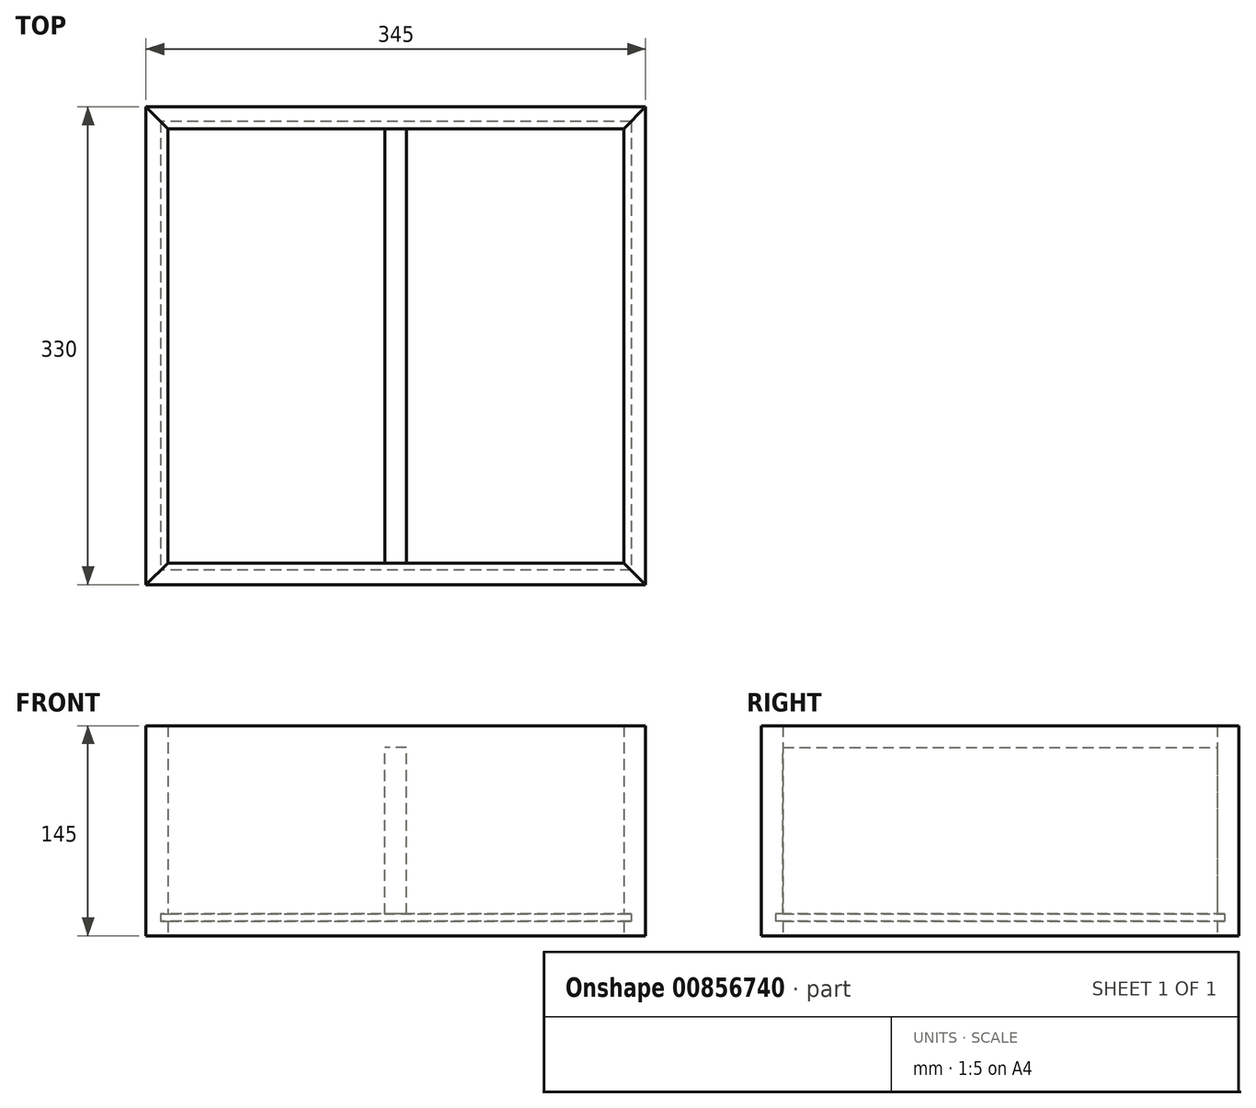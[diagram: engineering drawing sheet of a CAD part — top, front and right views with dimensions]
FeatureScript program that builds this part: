
annotation { "Feature Type Name" : "Feature", "Feature Type Description" : "" }
export const myFeature = defineFeature(function(context is Context, id is Id, definition is map)
    precondition{}
    {
        {
            var Q0;
            Q0=qCreatedBy(makeId("Front.planeOp"),FACE);
            var sketch = newSketch(context, id + "F0", { "sketchPlane" : qUnion([Q0])});
            skLineSegment(sketch, "E0", {"start": v(-172.5, 0) * mm, "end": v(172.5, 0) * mm, "construction": true});
            skLineSegment(sketch, "E1", {"start": v(172.5, 0) * mm, "end": v(172.5, 145) * mm, "construction": true});
            skLineSegment(sketch, "E2", {"start": v(172.5, 145) * mm, "end": v(-172.5, 145) * mm, "construction": true});
            skLineSegment(sketch, "E3", {"start": v(-172.5, 145) * mm, "end": v(-172.5, 0) * mm, "construction": true});
            skLineSegment(sketch, "E4", {"start": v(0, 145) * mm, "end": v(0, -38.8) * mm, "construction": true});
            skLineSegment(sketch, "E5", {"start": v(-172.5, 15) * mm, "end": v(172.5, 15) * mm, "construction": true});
            skLineSegment(sketch, "E6", {"start": v(-7.5, 130) * mm, "end": v(-7.5, 15) * mm, "construction": true});
            skLineSegment(sketch, "E7.MirrorCS", {"start": v(7.5, 130) * mm, "end": v(7.5, 15) * mm, "construction": true});
            skLineSegment(sketch, "E8", {"start": v(-157.5, 145) * mm, "end": v(-157.5, 0) * mm, "construction": true});
            skLineSegment(sketch, "E9", {"start": v(-7.5, 130) * mm, "end": v(7.5, 130) * mm, "construction": true});
            skLineSegment(sketch, "E10", {"start": v(-172.5, 130) * mm, "end": v(-157.5, 130) * mm, "construction": true});
            skLineSegment(sketch, "E11.MirrorCS", {"start": v(172.5, 130) * mm, "end": v(157.5, 130) * mm, "construction": true});
            skLineSegment(sketch, "E12.MirrorCS", {"start": v(157.5, 145) * mm, "end": v(157.5, 0) * mm, "construction": true});
            skLineSegment(sketch, "E13", {"start": v(-172.5, 10) * mm, "end": v(172.5, 10) * mm, "construction": true});
            skLineSegment(sketch, "E14", {"start": v(162.5, 15) * mm, "end": v(162.5, 10) * mm, "construction": true});
            skLineSegment(sketch, "E15.MirrorCS", {"start": v(-162.5, 15) * mm, "end": v(-162.5, 10) * mm, "construction": true});
            skSolve(sketch);
        }
        {
            var Q0;
            Q0=qCreatedBy(makeId("Right.planeOp"),FACE);
            var sketch = newSketch(context, id + "F1", { "sketchPlane" : qUnion([Q0])});
            skLineSegment(sketch, "E16", {"start": v(0, 0) * mm, "end": v(330, 0) * mm, "construction": true});
            skLineSegment(sketch, "E17", {"start": v(330, 0) * mm, "end": v(330, 145) * mm, "construction": true});
            skLineSegment(sketch, "E18", {"start": v(330, 145) * mm, "end": v(0, 145) * mm, "construction": true});
            skLineSegment(sketch, "E19", {"start": v(0, 130) * mm, "end": v(330, 130) * mm, "construction": true});
            skLineSegment(sketch, "E20", {"start": v(165, 145) * mm, "end": v(165, 0) * mm, "construction": true});
            skLineSegment(sketch, "E21", {"start": v(315, 145) * mm, "end": v(315, 0) * mm, "construction": true});
            skLineSegment(sketch, "E22.MirrorCS", {"start": v(15, 145) * mm, "end": v(15, 0) * mm, "construction": true});
            skLineSegment(sketch, "E23", {"start": v(330, 15) * mm, "end": v(0, 15) * mm, "construction": true});
            skLineSegment(sketch, "E24", {"start": v(330, 10) * mm, "end": v(0, 10) * mm, "construction": true});
            skLineSegment(sketch, "E25", {"start": v(320, 15) * mm, "end": v(320, 10) * mm, "construction": true});
            skLineSegment(sketch, "E26.MirrorCS", {"start": v(10, 15) * mm, "end": v(10, 10) * mm, "construction": true});
            skSolve(sketch);
        }
        {
            var Q0;
            Q0=qCreatedBy(makeId("Top.planeOp"),FACE);
            var Q1;
            Q1=sQuery(id+"F1.wireOp",VERTEX,"E25.end");
            cPlane(context, id + "F2", {"entities" : qUnion([Q0, Q1]), "cplaneType" : CPlaneType.PLANE_POINT, "offset" : 25 * mm, "width" : 150 * mm, "height" : 150 * mm});
        }
        {
            var Q0;
            Q0=qCreatedBy(id+"F2.planeOp",FACE);
            var sketch = newSketch(context, id + "F3", { "sketchPlane" : qUnion([Q0])});
            skLineSegment(sketch, "E27.bottom", {"start": v(162.5, 320) * mm, "end": v(-162.5, 320) * mm});
            skLineSegment(sketch, "E27.top", {"start": v(162.5, 10) * mm, "end": v(-162.5, 10) * mm});
            skLineSegment(sketch, "E27.left", {"start": v(162.5, 320) * mm, "end": v(162.5, 10) * mm});
            skLineSegment(sketch, "E27.right", {"start": v(-162.5, 320) * mm, "end": v(-162.5, 10) * mm});
            skSolve(sketch);
        }
        {
            var Q0;
            Q0 = qSketchRegion(id + "F3", true);
            var Q1;
            Q1=sQuery(id+"F1.wireOp",VERTEX,"E23.end");
            extrude(context, id + "F4", {"entities" : qUnion([Q0]), "endBound" : BoundingType.UP_TO_VERTEX, "depth" : 25 * mm, "endBoundEntityVertex" : qUnion([Q1]), "offsetDistance" : 25 * mm});
        }
        {
            var Q0;
            Q0=qCreatedBy(makeId("Top.planeOp"),FACE);
            var sketch = newSketch(context, id + "F5", { "sketchPlane" : qUnion([Q0])});
            skLineSegment(sketch, "E28", {"start": v(-172.5, 0) * mm, "end": v(-157.5, 15) * mm});
            skLineSegment(sketch, "E29", {"start": v(-157.5, 15) * mm, "end": v(157.5, 15) * mm});
            skLineSegment(sketch, "E30", {"start": v(157.5, 15) * mm, "end": v(172.5, 0) * mm});
            skLineSegment(sketch, "E31", {"start": v(172.5, 0) * mm, "end": v(-172.5, 0) * mm});
            skLineSegment(sketch, "E32", {"start": v(-225.32, 165) * mm, "end": v(297.83, 165) * mm, "construction": true});
            skLineSegment(sketch, "E33.MirrorCS", {"start": v(-157.5, 315) * mm, "end": v(157.5, 315) * mm});
            skLineSegment(sketch, "E34.MirrorCS", {"start": v(157.5, 315) * mm, "end": v(172.5, 330) * mm});
            skLineSegment(sketch, "E35.MirrorCS", {"start": v(172.5, 330) * mm, "end": v(-172.5, 330) * mm});
            skLineSegment(sketch, "E36.MirrorCS", {"start": v(-172.5, 330) * mm, "end": v(-157.5, 315) * mm});
            skLineSegment(sketch, "E37", {"start": v(-172.5, 0) * mm, "end": v(-172.5, 330) * mm});
            skLineSegment(sketch, "E38", {"start": v(-157.5, 315) * mm, "end": v(-157.5, 15) * mm});
            skLineSegment(sketch, "E39", {"start": v(172.5, 330) * mm, "end": v(172.5, 0) * mm});
            skLineSegment(sketch, "E40", {"start": v(157.5, 15) * mm, "end": v(157.5, 315) * mm});
            skSolve(sketch);
        }
        {
            var Q0;
            Q0=makeQuery(id+"F5.imprint","IMPRINT",FACE,{"disambiguationData":[TD([[makeQuery(id+"F5.imprint","IMPRINT",EDGE,{"derivedFrom":sQuery(id+"F5.wireOp",EDGE,"E28")}),1.0]])]});
            var Q1;
            Q1=makeQuery(id+"F5.imprint","IMPRINT",FACE,{"disambiguationData":[TD([[makeQuery(id+"F5.imprint","IMPRINT",EDGE,{"derivedFrom":sQuery(id+"F5.wireOp",EDGE,"E30")}),1.0]])]});
            var Q2;
            Q2=sQuery(id+"F0.wireOp",VERTEX,"E4.start");
            extrude(context, id + "F6", {"entities" : qUnion([Q0, Q1]), "endBound" : BoundingType.UP_TO_VERTEX, "depth" : 25 * mm, "endBoundEntityVertex" : qUnion([Q2]), "offsetDistance" : 25 * mm});
        }
        {
            var Q0;
            Q0=makeQuery(id+"F5.imprint","IMPRINT",FACE,{"disambiguationData":[TD([[makeQuery(id+"F5.imprint","IMPRINT",EDGE,{"derivedFrom":sQuery(id+"F5.wireOp",EDGE,"E33.MirrorCS")}),1.0]])]});
            var Q1;
            Q1=makeQuery(id+"F5.imprint","IMPRINT",FACE,{"disambiguationData":[TD([[makeQuery(id+"F5.imprint","IMPRINT",EDGE,{"derivedFrom":sQuery(id+"F5.wireOp",EDGE,"E28")}),-1.0]])]});
            var Q2;
            Q2=makeQuery(id+"F6.opExtrude","CAP_FACE",FACE,{"disambiguationData":[OSD([sQuery(id+"F5.wireOp",EDGE,"E30"),sQuery(id+"F5.wireOp",EDGE,"E34.MirrorCS"),sQuery(id+"F5.wireOp",EDGE,"E39"),sQuery(id+"F5.wireOp",EDGE,"E40")])],"isStart":false});
            extrude(context, id + "F7", {"entities" : qUnion([Q0, Q1]), "endBound" : BoundingType.UP_TO_SURFACE, "depth" : 25 * mm, "endBoundEntityFace" : qUnion([Q2]), "offsetDistance" : 25 * mm});
        }
        {
            var Q0;
            Q0=makeQuery(id+"F4.opExtrude","SWEPT_BODY",BODY,{"disambiguationData":[OSD([sQuery(id+"F3.wireOp",EDGE,"E27.bottom"),sQuery(id+"F3.wireOp",EDGE,"E27.top"),sQuery(id+"F3.wireOp",EDGE,"E27.left"),sQuery(id+"F3.wireOp",EDGE,"E27.right")])]});
            var Q1;
            Q1=makeQuery(id+"F6.opExtrude","SWEPT_BODY",BODY,{"disambiguationData":[OSD([sQuery(id+"F5.wireOp",EDGE,"E30"),sQuery(id+"F5.wireOp",EDGE,"E34.MirrorCS"),sQuery(id+"F5.wireOp",EDGE,"E39"),sQuery(id+"F5.wireOp",EDGE,"E40")])]});
            var Q2;
            Q2=makeQuery(id+"F6.opExtrude","SWEPT_BODY",BODY,{"disambiguationData":[OSD([sQuery(id+"F5.wireOp",EDGE,"E28"),sQuery(id+"F5.wireOp",EDGE,"E36.MirrorCS"),sQuery(id+"F5.wireOp",EDGE,"E37"),sQuery(id+"F5.wireOp",EDGE,"E38")])]});
            booleanBodies(context, id + "F8", {"operationType" : BooleanOperationType.SUBTRACTION, "tools" : qUnion([Q0]), "targets" : qUnion([Q1, Q2]), "oppositeDirection" : true, "keepTools" : true});
        }
        {
            var Q0;
            Q0=makeQuery(id+"F4.opExtrude","SWEPT_BODY",BODY,{"disambiguationData":[OSD([sQuery(id+"F3.wireOp",EDGE,"E27.bottom"),sQuery(id+"F3.wireOp",EDGE,"E27.top"),sQuery(id+"F3.wireOp",EDGE,"E27.left"),sQuery(id+"F3.wireOp",EDGE,"E27.right")])]});
            var Q1;
            Q1=makeQuery(id+"F7.opExtrude","SWEPT_BODY",BODY,{"disambiguationData":[OSD([sQuery(id+"F5.wireOp",EDGE,"E33.MirrorCS"),sQuery(id+"F5.wireOp",EDGE,"E34.MirrorCS"),sQuery(id+"F5.wireOp",EDGE,"E35.MirrorCS"),sQuery(id+"F5.wireOp",EDGE,"E36.MirrorCS")])]});
            var Q2;
            Q2=makeQuery(id+"F7.opExtrude","SWEPT_BODY",BODY,{"disambiguationData":[OSD([sQuery(id+"F5.wireOp",EDGE,"E28"),sQuery(id+"F5.wireOp",EDGE,"E29"),sQuery(id+"F5.wireOp",EDGE,"E30"),sQuery(id+"F5.wireOp",EDGE,"E31")])]});
            booleanBodies(context, id + "F9", {"operationType" : BooleanOperationType.SUBTRACTION, "tools" : qUnion([Q0]), "targets" : qUnion([Q1, Q2]), "keepTools" : true});
        }
        {
            var Q0;
            {var subQ2=sQuery(id+"F5.wireOp",EDGE,"E33.MirrorCS");Q0=makeQuery(id+"F9.opBoolean","SPLIT",FACE,{"disambiguationData":[TD([makeQuery(id+"F4.opExtrude","CAP_FACE",FACE,{"disambiguationData":[OSD([sQuery(id+"F3.wireOp",EDGE,"E27.bottom"),sQuery(id+"F3.wireOp",EDGE,"E27.top"),sQuery(id+"F3.wireOp",EDGE,"E27.left"),sQuery(id+"F3.wireOp",EDGE,"E27.right")])],"isStart":false})])],"derivedFrom":makeQuery(id+"F7.opExtrude","SWEPT_FACE",FACE,{"disambiguationData":[OSD([subQ2])]})});}
            var sketch = newSketch(context, id + "F10", { "sketchPlane" : qUnion([Q0])});
            skLineSegment(sketch, "E41.bottom", {"start": v(-7.5, 130) * mm, "end": v(7.5, 130) * mm});
            skLineSegment(sketch, "E41.top", {"start": v(-7.5, 15) * mm, "end": v(7.5, 15) * mm});
            skLineSegment(sketch, "E41.left", {"start": v(-7.5, 130) * mm, "end": v(-7.5, 15) * mm});
            skLineSegment(sketch, "E41.right", {"start": v(7.5, 130) * mm, "end": v(7.5, 15) * mm});
            skSolve(sketch);
        }
        {
            var Q0;
            Q0 = qSketchRegion(id + "F10", true);
            var Q1;
            {var subQ2=sQuery(id+"F5.wireOp",EDGE,"E29");Q1=makeQuery(id+"F9.opBoolean","SPLIT",FACE,{"disambiguationData":[TD([makeQuery(id+"F4.opExtrude","CAP_FACE",FACE,{"disambiguationData":[OSD([sQuery(id+"F3.wireOp",EDGE,"E27.bottom"),sQuery(id+"F3.wireOp",EDGE,"E27.top"),sQuery(id+"F3.wireOp",EDGE,"E27.left"),sQuery(id+"F3.wireOp",EDGE,"E27.right")])],"isStart":true})])],"derivedFrom":makeQuery(id+"F7.opExtrude","SWEPT_FACE",FACE,{"disambiguationData":[OSD([subQ2])]})});}
            extrude(context, id + "F11", {"entities" : qUnion([Q0]), "endBound" : BoundingType.UP_TO_SURFACE, "depth" : 25 * mm, "endBoundEntityFace" : qUnion([Q1]), "offsetDistance" : 25 * mm});
        }
    });
